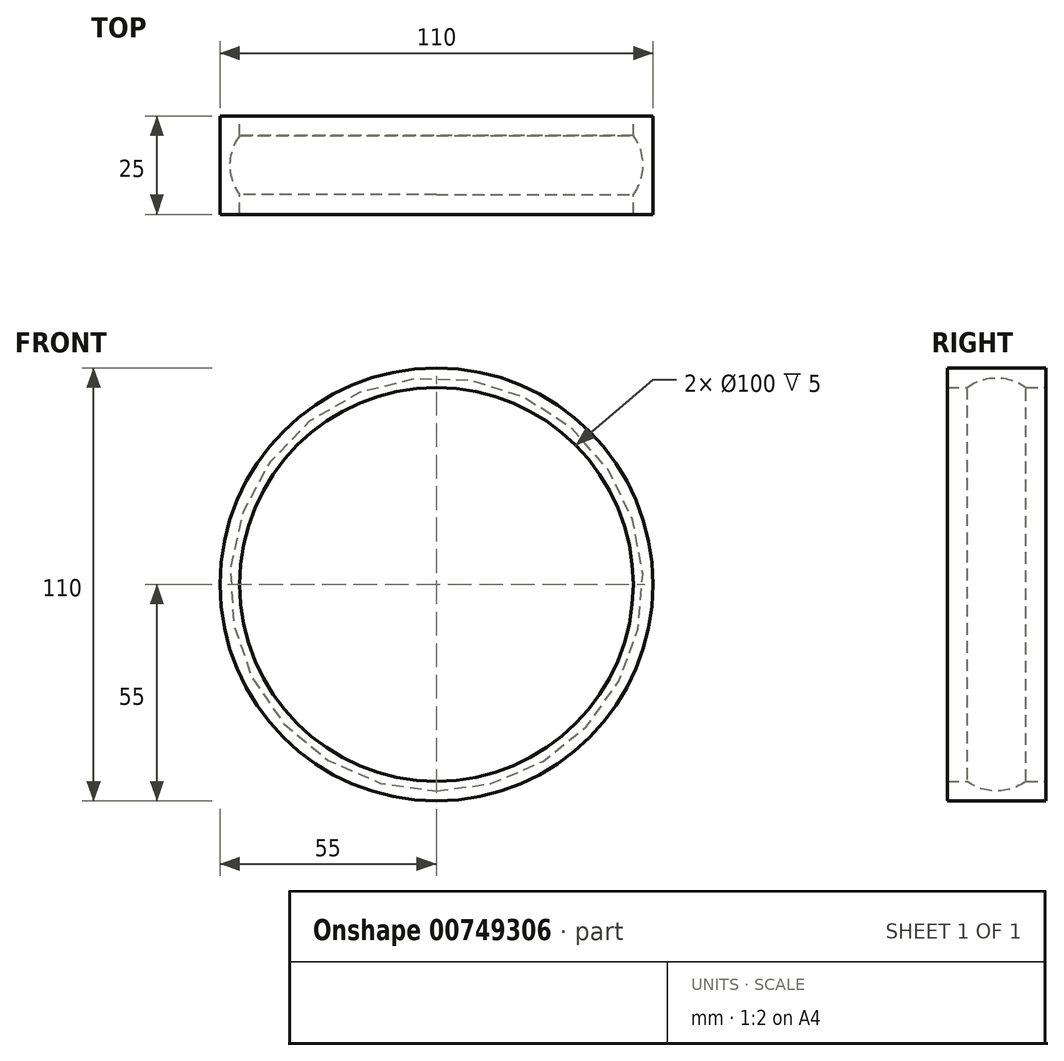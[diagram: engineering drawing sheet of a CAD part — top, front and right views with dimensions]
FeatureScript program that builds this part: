
annotation { "Feature Type Name" : "Feature", "Feature Type Description" : "" }
export const myFeature = defineFeature(function(context is Context, id is Id, definition is map)
    precondition{}
    {
        {
            var Q0;
            Q0=qCreatedBy(makeId("Front.planeOp"),FACE);
            var sketch = newSketch(context, id + "F0", { "sketchPlane" : qUnion([Q0])});
            skCircle(sketch, "E0", {"center": v(0, 0) * mm, "radius": 50 * mm});
            skCircle(sketch, "E1", {"center": v(0, 0) * mm, "radius": 55 * mm});
            skCircle(sketch, "E2", {"center": v(0, 0) * mm, "radius": 30 * mm});
            skLineSegment(sketch, "E3", {"start": v(0, 30) * mm, "end": v(0, 50) * mm});
            skSolve(sketch);
        }
        {
            var Q0;
            Q0=makeQuery(id+"F0.imprint","IMPRINT",FACE,{"disambiguationData":[TD([[makeQuery(id+"F0.imprint","IMPRINT",EDGE,{"derivedFrom":sQuery(id+"F0.wireOp",EDGE,"E0")}),-1.0]])]});
            extrude(context, id + "F1", {"entities" : qUnion([Q0]), "depth" : 25 * mm, "offsetDistance" : 25 * mm, "symmetric" : true});
        }
        {
            var Q0;
            Q0=qCreatedBy(makeId("Right.planeOp"),FACE);
            var sketch = newSketch(context, id + "F2", { "sketchPlane" : qUnion([Q0])});
            skArc(sketch, "E4", {"start": v(12.5, 40) * mm, "mid": v(0, 52.5) * mm, "end": v(-12.5, 40) * mm});
            skLineSegment(sketch, "E5", {"start": v(-12.5, 40) * mm, "end": v(12.5, 40) * mm});
            skSolve(sketch);
        }
        {
            var Q0;
            Q0=makeQuery(id+"F2.imprint","IMPRINT",FACE,{"disambiguationData":[TD([[makeQuery(id+"F2.imprint","IMPRINT",EDGE,{"derivedFrom":sQuery(id+"F2.wireOp",EDGE,"E4")}),1.0]])]});
            var Q1;
            Q1=sQuery(id+"F0.wireOp",EDGE,"E0");
            revolve(context, id + "F3", {"operationType" : NewBodyOperationType.REMOVE, "surfaceOperationType" : NewSurfaceOperationType.NEW, "entities" : qUnion([Q0]), "axis" : qUnion([Q1]), "revolveType" : RevolveType.FULL, "oppositeDirection" : true});
        }
    });
